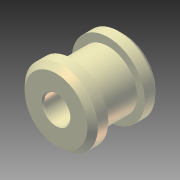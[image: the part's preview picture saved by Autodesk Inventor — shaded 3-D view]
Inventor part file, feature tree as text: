
AUTODESK INVENTOR PART (.ipt)
format: ipt  version: 2015 (Build 190159000, 159)  size: 113,152 bytes
history: native  units: mm
features: chamfer x2, revolve x1
ambient origin geometry x8: Origin, YZ Plane, XZ Plane, XY Plane, X Axis, Y Axis, Z Axis, Center Point
bodies: Solid1 (feature_tree)
feature tree (3):
  revolve  "Revolución1"  [1 undecoded]
  chamfer  "Chaflán1"  Distance=13.0mm
  chamfer  "Chaflán2"  Distance=14.0mm
note: 1 required parameter value undecoded (feature->parameter linkage not recoverable at this tier; creation-order binding heuristic only, values carry confidence <= 0.55)
